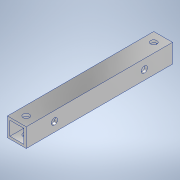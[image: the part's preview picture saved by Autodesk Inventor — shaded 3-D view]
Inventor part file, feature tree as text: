
AUTODESK INVENTOR PART (.ipt)
format: ipt  version: 2020.3 (Build 243373000, 373)  size: 130,560 bytes
history: native  units: mm
features: sketch x3, hole x2, other x1, extrude x1
ambient origin geometry x8: Origin, YZ Plane, XZ Plane, XY Plane, X Axis, Y Axis, Z Axis, Center Point
bodies: Body1 (feature_tree)
feature tree (7):
  other  "ソリッド1"
  extrude  "押し出し1"  Depth=9.0mm
  hole  "穴2"  [1 undecoded]
  hole  "穴3"  [1 undecoded]
  sketch  "スケッチ1"
  sketch  "スケッチ3"
  sketch  "スケッチ4"
note: 2 required parameter values undecoded (feature->parameter linkage not recoverable at this tier; creation-order binding heuristic only, values carry confidence <= 0.55)
